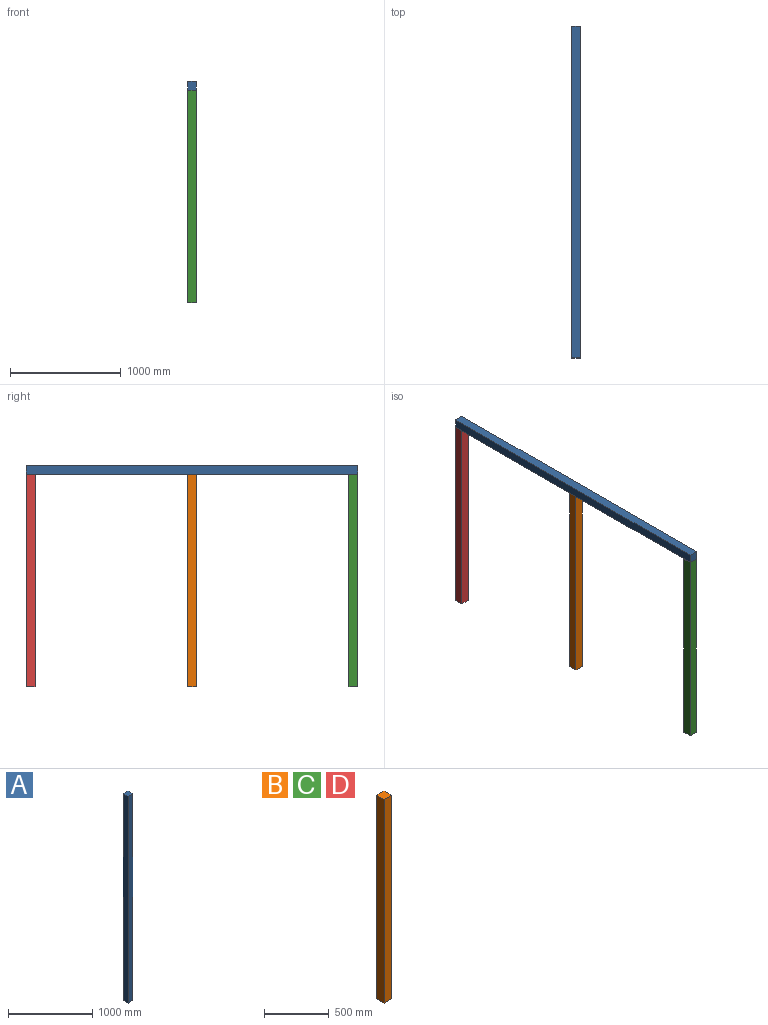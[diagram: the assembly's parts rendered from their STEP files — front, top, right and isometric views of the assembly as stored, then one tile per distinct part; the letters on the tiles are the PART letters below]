
ASSEMBLY  parts=4 mates=3
PART A: 6 faces, bbox 80x80x3000 mm
  f0: plane 3000x80mm, normal (0,1,0), area 240000mm2, adj f1,f3,f4,f5
  f1: plane 3000x80mm, normal (-1,0,0), area 240000mm2, adj f0,f2,f4,f5
  f2: plane 3000x80mm, normal (0,-1,0), area 240000mm2, adj f1,f3,f4,f5
  f3: plane 3000x80mm, normal (1,0,0), area 240000mm2, adj f0,f2,f4,f5
  f4: plane 80x80mm, normal (0,0,1), area 6400mm2, adj f0,f1,f2,f3
  f5: plane 80x80mm, normal (0,0,-1), area 6400mm2, adj f0,f1,f2,f3
PART B: 6 faces, bbox 80x80x1920 mm
  f0: plane 1920x80mm, normal (0,1,0), area 153600mm2, adj f1,f3,f4,f5
  f1: plane 1920x80mm, normal (-1,0,0), area 153600mm2, adj f0,f2,f4,f5
  f2: plane 1920x80mm, normal (0,-1,0), area 153600mm2, adj f1,f3,f4,f5
  f3: plane 1920x80mm, normal (1,0,0), area 153600mm2, adj f0,f2,f4,f5
  f4: plane 80x80mm, normal (0,0,1), area 6400mm2, adj f0,f1,f2,f3
  f5: plane 80x80mm, normal (0,0,-1), area 6400mm2, adj f0,f1,f2,f3
PART C: same geometry as B
PART D: same geometry as B
PLACE A rot(axis=(1,0,0),90deg) t=(-232.66,698.55,1222.93)mm
PLACE B t=(-232.66,-801.45,-737.07)mm
PLACE C t=(-232.66,-2261.45,-737.07)mm
PLACE D t=(-232.66,658.55,-737.07)mm
MATE planar B.f4 <-> A.f2  axis (0,0,1) through (-232.66,-801.45,1182.93)mm
MATE planar A.f2 <-> C.f4  axis (0,0,-1) through (-232.66,-801.45,1182.93)mm
MATE planar D.f4 <-> A.f2  axis (0,0,1) through (-232.66,658.55,1182.93)mm
